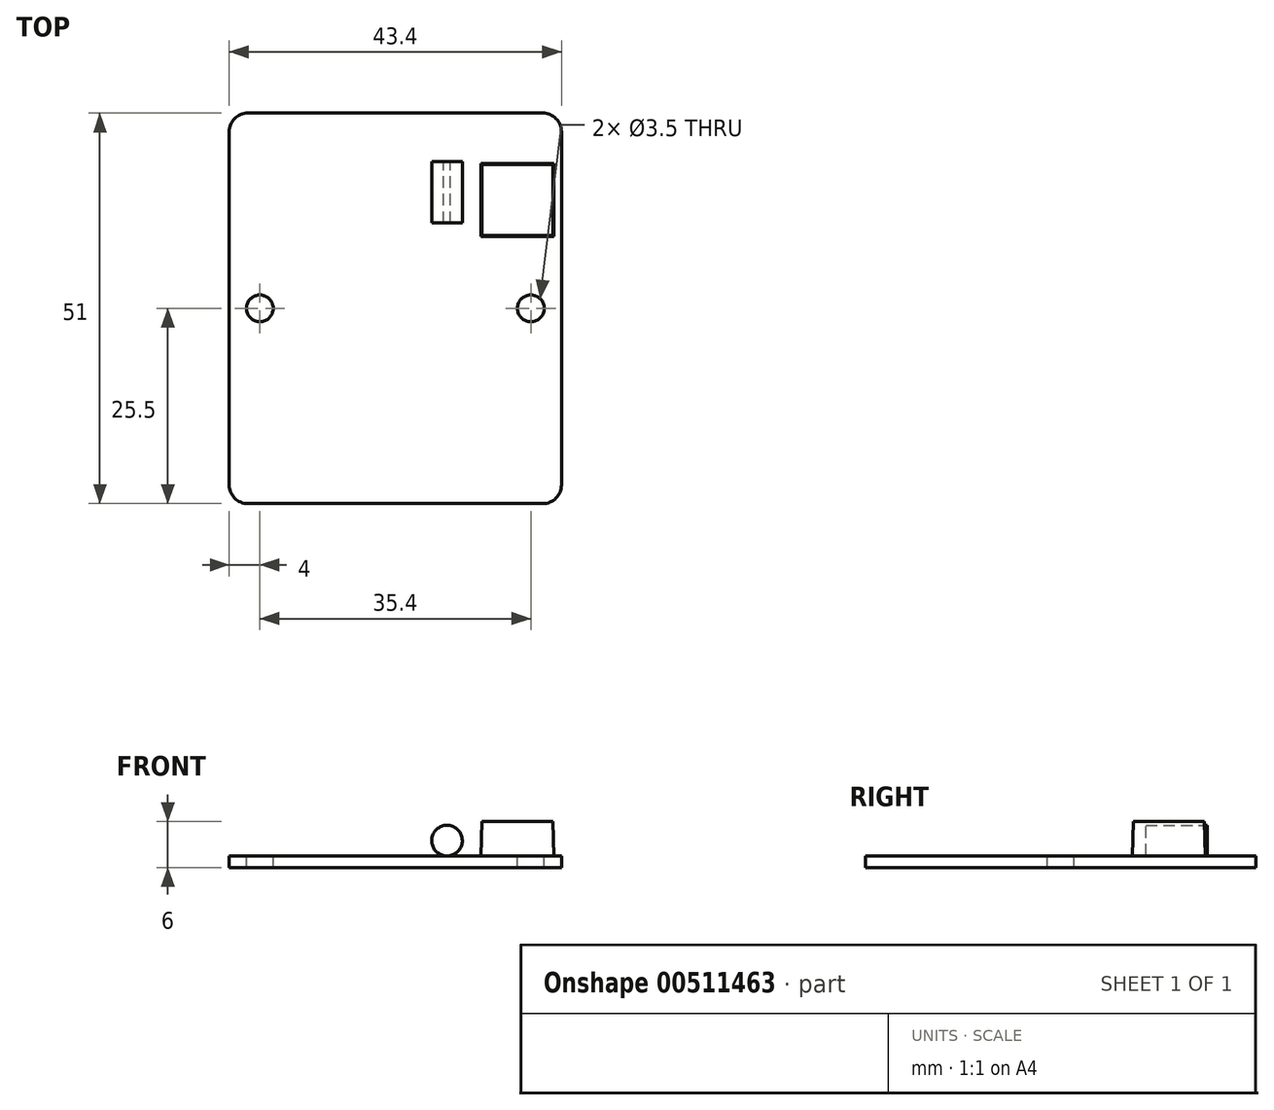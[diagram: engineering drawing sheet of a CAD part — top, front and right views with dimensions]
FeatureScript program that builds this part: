
annotation { "Feature Type Name" : "Feature", "Feature Type Description" : "" }
export const myFeature = defineFeature(function(context is Context, id is Id, definition is map)
    precondition{}
    {
        {
            var Q0;
            Q0=qCreatedBy(makeId("Top.planeOp"),FACE);
            var sketch = newSketch(context, id + "F0", { "sketchPlane" : qUnion([Q0])});
            skLineSegment(sketch, "E0.bottom", {"start": v(21.7, 25.5) * mm, "end": v(-21.7, 25.5) * mm});
            skLineSegment(sketch, "E0.top", {"start": v(21.7, -25.5) * mm, "end": v(-21.7, -25.5) * mm});
            skLineSegment(sketch, "E0.left", {"start": v(21.7, 25.5) * mm, "end": v(21.7, -25.5) * mm});
            skLineSegment(sketch, "E0.right", {"start": v(-21.7, 25.5) * mm, "end": v(-21.7, -25.5) * mm});
            skPoint(sketch, "E0.middle", {"position": v(0, 0) * mm});
            skSolve(sketch);
        }
        {
            var Q0;
            Q0=makeQuery(id+"F0.imprint","IMPRINT",FACE,{"disambiguationData":[TD([[makeQuery(id+"F0.imprint","IMPRINT",EDGE,{"derivedFrom":sQuery(id+"F0.wireOp",EDGE,"E0.bottom")}),1.0]])]});
            extrude(context, id + "F1", {"entities" : qUnion([Q0]), "depth" : 1.5 * mm, "offsetDistance" : 25 * mm});
        }
        {
            var Q0;
            Q0=makeQuery(id+"F1.opExtrude","SWEPT_EDGE",EDGE,{"disambiguationData":[OSD([sQuery(id+"F0.wireOp",EDGE,"E0.bottom"),sQuery(id+"F0.wireOp",EDGE,"E0.right")])]});
            var Q1;
            Q1=makeQuery(id+"F1.opExtrude","SWEPT_EDGE",EDGE,{"disambiguationData":[OSD([sQuery(id+"F0.wireOp",EDGE,"E0.bottom"),sQuery(id+"F0.wireOp",EDGE,"E0.left")])]});
            var Q2;
            Q2=makeQuery(id+"F1.opExtrude","SWEPT_EDGE",EDGE,{"disambiguationData":[OSD([sQuery(id+"F0.wireOp",EDGE,"E0.top"),sQuery(id+"F0.wireOp",EDGE,"E0.left")])]});
            var Q3;
            Q3=makeQuery(id+"F1.opExtrude","SWEPT_EDGE",EDGE,{"disambiguationData":[OSD([sQuery(id+"F0.wireOp",EDGE,"E0.top"),sQuery(id+"F0.wireOp",EDGE,"E0.right")])]});
            fillet(context, id + "F2", {"entities" : qUnion([Q0, Q1, Q2, Q3]), "tangentPropagation" : true, "radius" : 2.45 * mm, "defaultsChanged" : false, "vertexSettings" : [], "allowEdgeOverflow" : false});
        }
        {
            var Q0;
            Q0=makeQuery(id+"F1.opExtrude","CAP_FACE",FACE,{"disambiguationData":[OSD([sQuery(id+"F0.wireOp",EDGE,"E0.bottom"),sQuery(id+"F0.wireOp",EDGE,"E0.top"),sQuery(id+"F0.wireOp",EDGE,"E0.left"),sQuery(id+"F0.wireOp",EDGE,"E0.right")])],"isStart":false});
            var sketch = newSketch(context, id + "F3", { "sketchPlane" : qUnion([Q0])});
            skLineSegment(sketch, "E1", {"start": v(17.7, 0) * mm, "end": v(-17.7, 0) * mm, "construction": true});
            skPoint(sketch, "E2", {"position": v(0, 0) * mm});
            skCircle(sketch, "E3", {"center": v(-17.7, 0) * mm, "radius": 1.75 * mm});
            skCircle(sketch, "E4", {"center": v(17.7, 0) * mm, "radius": 1.75 * mm});
            skSolve(sketch);
        }
        {
            var Q0;
            Q0=qSketchRegion(id+"F3",true);
            extrude(context, id + "F4", {"entities" : qUnion([Q0]), "operationType" : NewBodyOperationType.REMOVE, "endBound" : BoundingType.THROUGH_ALL, "oppositeDirection" : true, "depth" : 25 * mm, "offsetDistance" : 25 * mm});
        }
        {
            var Q0;
            Q0=makeQuery(id+"F1.opExtrude","CAP_FACE",FACE,{"disambiguationData":[OSD([sQuery(id+"F0.wireOp",EDGE,"E0.bottom"),sQuery(id+"F0.wireOp",EDGE,"E0.top"),sQuery(id+"F0.wireOp",EDGE,"E0.left"),sQuery(id+"F0.wireOp",EDGE,"E0.right")])],"isStart":false});
            var sketch = newSketch(context, id + "F5", { "sketchPlane" : qUnion([Q0])});
            skLineSegment(sketch, "E5.bottom", {"start": v(20.7, 18.9) * mm, "end": v(11.2, 18.9) * mm});
            skLineSegment(sketch, "E5.top", {"start": v(20.7, 9.4) * mm, "end": v(11.2, 9.4) * mm});
            skLineSegment(sketch, "E5.left", {"start": v(20.7, 18.9) * mm, "end": v(20.7, 9.4) * mm});
            skLineSegment(sketch, "E5.right", {"start": v(11.2, 18.9) * mm, "end": v(11.2, 9.4) * mm});
            skSolve(sketch);
        }
        {
            var Q0;
            Q0=qSketchRegion(id+"F5",true);
            extrude(context, id + "F6", {"entities" : qUnion([Q0]), "operationType" : NewBodyOperationType.ADD, "depth" : 4.5 * mm, "offsetDistance" : 25 * mm, "hasDraft" : true, "draftAngle" : 1.5 * degree, "draftPullDirection" : true});
        }
        {
            var Q0;
            Q0=makeQuery(id+"F1.opExtrude","CAP_FACE",FACE,{"disambiguationData":[OSD([sQuery(id+"F0.wireOp",EDGE,"E0.bottom"),sQuery(id+"F0.wireOp",EDGE,"E0.top"),sQuery(id+"F0.wireOp",EDGE,"E0.left"),sQuery(id+"F0.wireOp",EDGE,"E0.right")])],"isStart":false});
            var sketch = newSketch(context, id + "F7", { "sketchPlane" : qUnion([Q0])});
            skLineSegment(sketch, "E6.bottom", {"start": v(-19.7, -17.6) * mm, "end": v(-11.85, -17.6) * mm});
            skLineSegment(sketch, "E6.top", {"start": v(-19.7, -22.55) * mm, "end": v(-11.85, -22.55) * mm});
            skLineSegment(sketch, "E6.left", {"start": v(-19.7, -17.6) * mm, "end": v(-19.7, -22.55) * mm});
            skLineSegment(sketch, "E6.right", {"start": v(-11.85, -17.6) * mm, "end": v(-11.85, -22.55) * mm});
            skSolve(sketch);
        }
        {
            var Q0;
            Q0=qSketchRegion(id+"F7",true);
            extrude(context, id + "F8", {"entities" : qUnion([Q0]), "operationType" : NewBodyOperationType.ADD, "depth" : 8.5 * mm, "offsetDistance" : 25 * mm});
        }
        {
            var Q0;
            Q0=makeQuery(id+"F1.opExtrude","CAP_FACE",FACE,{"disambiguationData":[OSD([sQuery(id+"F0.wireOp",EDGE,"E0.bottom"),sQuery(id+"F0.wireOp",EDGE,"E0.top"),sQuery(id+"F0.wireOp",EDGE,"E0.left"),sQuery(id+"F0.wireOp",EDGE,"E0.right")])],"isStart":false});
            var sketch = newSketch(context, id + "F9", { "sketchPlane" : qUnion([Q0])});
            skLineSegment(sketch, "E7.bottom", {"start": v(4.6, 19.15) * mm, "end": v(8.85, 19.15) * mm});
            skLineSegment(sketch, "E7.top", {"start": v(4.6, 11.15) * mm, "end": v(8.85, 11.15) * mm});
            skLineSegment(sketch, "E7.left", {"start": v(4.6, 19.15) * mm, "end": v(4.6, 11.15) * mm});
            skLineSegment(sketch, "E7.right", {"start": v(8.85, 19.15) * mm, "end": v(8.85, 11.15) * mm});
            skSolve(sketch);
        }
        {
            var Q0;
            Q0=qSketchRegion(id+"F9",true);
            extrude(context, id + "F10", {"entities" : qUnion([Q0]), "operationType" : NewBodyOperationType.ADD, "depth" : (5.65 - 1.5) * mm, "offsetDistance" : 25 * mm});
        }
        {
            var Q0;
            Q0=makeQuery(id+"F10.opExtrude","SWEPT_FACE",FACE,{"disambiguationData":[OSD([sQuery(id+"F9.wireOp",EDGE,"E7.bottom")])]});
            var sketch = newSketch(context, id + "F11", { "sketchPlane" : qUnion([Q0])});
            skCircle(sketch, "E8", {"center": v(-6.75, 3.5) * mm, "radius": 2 * mm});
            skLineSegment(sketch, "E9.bottom", {"start": v(-7.2, 1.55) * mm, "end": v(-6.3, 1.55) * mm});
            skLineSegment(sketch, "E9.top", {"start": v(-7.2, 1.5) * mm, "end": v(-6.3, 1.5) * mm});
            skLineSegment(sketch, "E9.left", {"start": v(-7.2, 1.55) * mm, "end": v(-7.2, 1.5) * mm});
            skLineSegment(sketch, "E9.right", {"start": v(-6.3, 1.55) * mm, "end": v(-6.3, 1.5) * mm});
            skSolve(sketch);
        }
        {
            var Q0;
            {var subQ2=sQuery(id+"F11.wireOp",EDGE,"E9.left");Q0=makeQuery(id+"F11.imprint","IMPRINT",FACE,{"disambiguationData":[TD([[makeQuery(id+"F11.imprint","IMPRINT",EDGE,{"derivedFrom":subQ2}),-1.0]])]});}
            extrude(context, id + "F12", {"entities" : qUnion([Q0]), "operationType" : NewBodyOperationType.REMOVE, "endBound" : BoundingType.THROUGH_ALL, "oppositeDirection" : true, "depth" : 25 * mm, "offsetDistance" : 25 * mm});
        }
        {
            var Q0;
            Q0=makeQuery(id+"F8.opExtrude","CAP_FACE",FACE,{"disambiguationData":[OSD([sQuery(id+"F7.wireOp",EDGE,"E6.bottom"),sQuery(id+"F7.wireOp",EDGE,"E6.top"),sQuery(id+"F7.wireOp",EDGE,"E6.left"),sQuery(id+"F7.wireOp",EDGE,"E6.right")])],"isStart":false});
            var Q1;
            {var subQ0=sQuery(id+"F9.wireOp",EDGE,"E7.bottom");var subQ1=makeQuery(id+"F10.opExtrude","CAP_EDGE",EDGE,{"disambiguationData":[OSD([subQ0])],"isStart":true});Q1=makeQuery(id+"F12.boolean.opBoolean","MERGE",FACE,{"derivedFrom":[makeQuery(id+"F1.opExtrude","CAP_FACE",FACE,{"disambiguationData":[OSD([sQuery(id+"F0.wireOp",EDGE,"E0.bottom"),sQuery(id+"F0.wireOp",EDGE,"E0.top"),sQuery(id+"F0.wireOp",EDGE,"E0.left"),sQuery(id+"F0.wireOp",EDGE,"E0.right")])],"isStart":false})],"fromTools":[makeQuery(id+"F12.opExtrude","SWEPT_FACE",FACE,{"disambiguationData":[OSD([subQ0]),TDD([makeQuery(id+"F11.imprint","IMPRINT",EDGE,{"disambiguationData":[TD([[makeQuery(id+"F11.imprint","INTERSECT",VERTEX,{"derivedFrom":[makeQuery(id+"F10.opExtrude","SWEPT_EDGE",EDGE,{"disambiguationData":[OSD([subQ0,sQuery(id+"F9.wireOp",EDGE,"E7.left")])]}),subQ1]}),-1.0]])],"derivedFrom":subQ1})])]}),makeQuery(id+"F12.opExtrude","SWEPT_FACE",FACE,{"disambiguationData":[OSD([subQ0]),TDD([makeQuery(id+"F11.imprint","IMPRINT",EDGE,{"disambiguationData":[TD([[makeQuery(id+"F11.imprint","INTERSECT",VERTEX,{"derivedFrom":[makeQuery(id+"F10.opExtrude","SWEPT_EDGE",EDGE,{"disambiguationData":[OSD([subQ0,sQuery(id+"F9.wireOp",EDGE,"E7.right")])]}),subQ1]}),1.0]])],"derivedFrom":subQ1})])]})]});}
            extrude(context, id + "F13", {"entities" : qUnion([Q0]), "operationType" : NewBodyOperationType.REMOVE, "endBound" : BoundingType.UP_TO_SURFACE, "oppositeDirection" : true, "depth" : 25 * mm, "endBoundEntityFace" : qUnion([Q1]), "offsetDistance" : 25 * mm});
        }
    });
